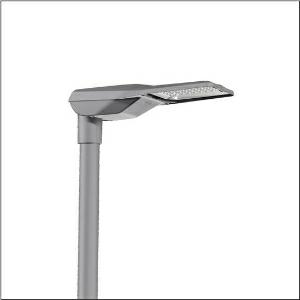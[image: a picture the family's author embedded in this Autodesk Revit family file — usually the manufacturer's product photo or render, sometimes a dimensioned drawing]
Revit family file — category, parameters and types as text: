
# Revit family: streetlight_sl_21_iq_mini___st0_8a_5xe2c31d08gb_9b37
name_source: partatom
category: Lighting Fixtures
units: mm (PartAtom-declared; Revit-internal decimal feet)

## family parameters
Cut with Voids When Loaded = No
Host = Face
Light Source = No
Part Type = Normal
Room Calculation Point = No
Round Connector Dimension = Use Diameter
Shared = No

## types (1)
- --- (1 x LED, 5680 lm, 37.1 W, 3000K)
    Apparent Load = 37 VA
    CIE Flux Codes = 38 75 97 100 100
    Color Rendering = 70
    Color Temperature = 3000K
    Default Elevation = 1800 mm
    Description = Streetlight SL 21 iQ mini, mast luminaire, primary light control with lens, of PMMA, primary optical cover: cover, of toughened safety glass, transparent, light distribution: ST0.8a, light emission: direct distribution, primary light characteristic: asymmetric, installation type: post-top, side-entry, LED, High Power LED, rated luminous flux: 5.680lm, luminous efficacy: 153lm/W, light colour: 730, colour temperature: 3000K, control gear: iQ-Comfort, control: Auto-Match, Temp-Guard, Lumen-Switch, Night-Set, Smart-Wire, Light-Fading, Desk-Remote (wireless, voltage-free reading and setting of iQ features in the workshop via application-optimized NFC function/RFID function), optimised constant luminous flux control (CLO 2.0), pre-setting: linear dimming characteristic, mains connection: 220..240V, AC, 50/60Hz, start of lifetime: 37W, end of service life: 39W, reduction: 18W, luminaire housing, of diecast aluminium, powder-coated, SITECO metallic grey (DB 702S), corrosivity category C5 high according to DIN EN ISO 12944, please order mast flange separately, inclination adjustable: 0°, 5°, 10°, 15°, sealing non-destructively replaceable, multi-level sealing system, length: 628mm, width: 235mm, height: 110mm, mast flange for spigot size: 42mm (side-entry): 5XC10008XM4, 60/48mm (side-entry/post-top): 5XC10108XM2, 76/60mm (side-entry/post-top): 5XC10108XM1, mounting height: 4..8m, protection rating (complete): IP66, insulation class (complete): insulation class II (safety insulation), certification: CE, ENEC, ENEC+, VDE, impact resistance: IK10, permissible operating ambient temperature for outdoor applications: -40..+50°C, standard-compliant lighting for roads and squares, packaging unit: 1 piece

Light Distribution: ST0.8a
    Height = 110 mm
    Lamp = 1 x LED
    Lamp Light Flux = 5680 lm
    Lamp Power = 37.1 W
    Lamp count = 1
    Length = 625 mm
    Luminous efficacy = 153 lm/W
    Manufacturer = Siteco
    ModVariant = No
    Model = 5XE2C31D08GB
    Number of Poles = 1
    OnlyDefault = Yes
    Power Factor = 1
    Product Name = Streetlight SL 21 iQ mini | ST0.8a
    Product group = mast luminaire | pylon top
    ProductGroupID = 6100
    Protection Class = Protection class II
    Protection Degree = IP 66
    RLX_Detail_Level = 1
    RLX_Emergency_Light_Flux = 0 lm
    RLX_Emergency_Type = 0
    RLX_Emergency_Type_DB = No
    RlxData = <blob elided: 26409 chars, md5=ed4cafef>
    Socket = socket
    Standby Power = 0 W
    System Light Flux = 5680 lm
    System Power = 37 W
    Type Comments = factory setting: luminous flux: 100 % | dim-lin: 254 | 385 mA
    Type Image = l_1003519.jpg
    URL = http://relux.com
    VarID = @adj_183181
    Voltage = 0 V
    Weight = 0.00 kg
    Width = 234 mm

## geometry (parser evidence)
native form markers: Blend x4, Sweep x9
no freeform markers — native parametric forms only
